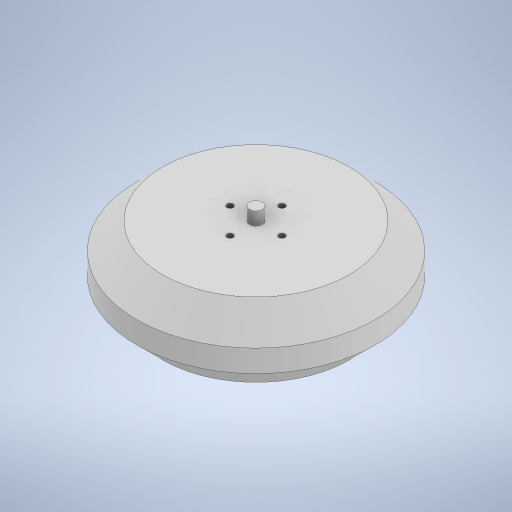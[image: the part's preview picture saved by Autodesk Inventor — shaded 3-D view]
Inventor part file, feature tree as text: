
AUTODESK INVENTOR PART (.ipt)
format: ipt  version: 2023 (Build 270158030, 158C)  size: 249,856 bytes
history: native  units: in
note: dims shown in document units (in); Inventor stores cm internally (conversion verified against a paired STEP export)
features: sketch x3, extrude x2, chamfer x1, hole x1
ambient origin geometry x8: Origin, YZ Plane, XZ Plane, XY Plane, X Axis, Y Axis, Z Axis, Center Point
bodies: Solid1 (feature_tree)
feature tree (7):
  extrude  "Extrusion1"  Depth=0.3937in
  chamfer  "Chamfer1"  Distance=0.3937in Angle=45.0deg
  hole  "Hole1"  [1 undecoded]
  extrude  "Extrusion2"  Depth=0.1969in TaperAngle=0.0deg
  sketch  "Sketch1"  dims[d0=1.122in d1=0.0in d2=3.622in d3=0.3937in d4=0.0787in d5=45.0deg]
  sketch  "Sketch2"  dims[d6=0.0968in d7=0.2362in d8=0.1575in d9=0.0787in d10=90.0deg d11=0.3465in d12=0.8108in d13=0.7874in]
  sketch  "Sketch3"  dims[d14=0.1969in d15=0.1969in d16=0.0in]
note: 1 required parameter value undecoded (feature->parameter linkage not recoverable at this tier; creation-order binding heuristic only, values carry confidence <= 0.55)
